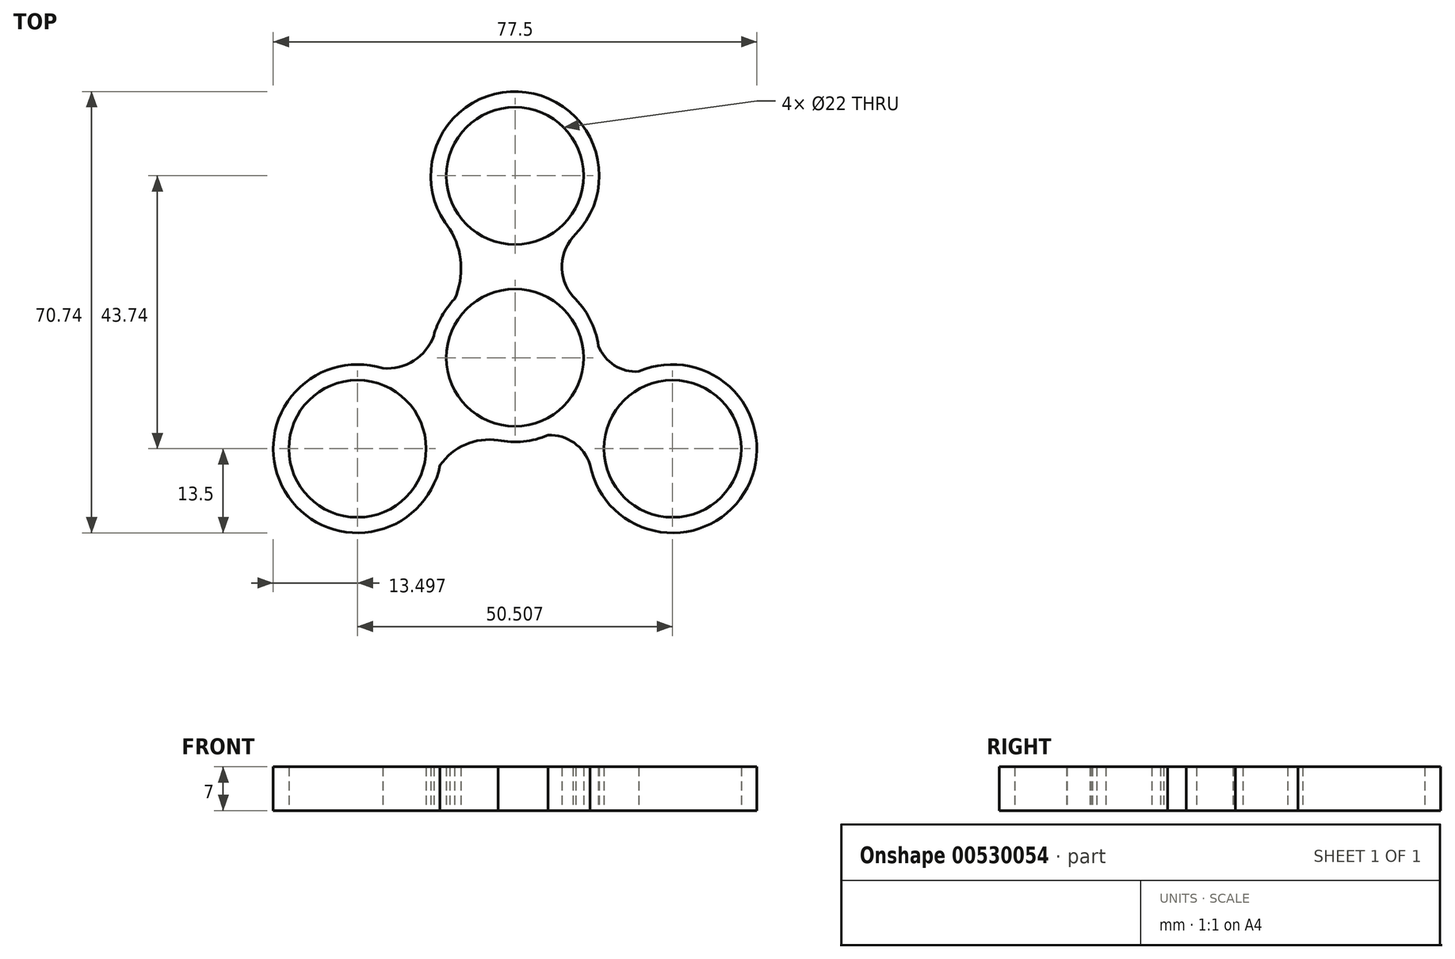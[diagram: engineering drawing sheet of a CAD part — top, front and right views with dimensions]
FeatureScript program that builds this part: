
annotation { "Feature Type Name" : "Feature", "Feature Type Description" : "" }
export const myFeature = defineFeature(function(context is Context, id is Id, definition is map)
    precondition{}
    {
        {
            var Q0;
            Q0=qCreatedBy(makeId("Top.planeOp"),FACE);
            var sketch = newSketch(context, id + "F0", { "sketchPlane" : qUnion([Q0])});
            skCircle(sketch, "E0", {"center": v(0, 0) * mm, "radius": 11 * mm});
            skCircle(sketch, "E1", {"center": v(0, 0) * mm, "radius": 13.5 * mm});
            skCircle(sketch, "E2", {"center": v(0, 29.16) * mm, "radius": 11 * mm});
            skCircle(sketch, "E3", {"center": v(0, 29.16) * mm, "radius": 13.5 * mm});
            skCircle(sketch, "E4.1.0", {"center": v(-25.25, -14.58) * mm, "radius": 11 * mm});
            skCircle(sketch, "E4.2.0", {"center": v(25.25, -14.58) * mm, "radius": 11 * mm});
            skCircle(sketch, "E5.1.0", {"center": v(-25.25, -14.58) * mm, "radius": 13.5 * mm});
            skCircle(sketch, "E5.2.0", {"center": v(25.25, -14.58) * mm, "radius": 13.5 * mm});
            skArc(sketch, "E6", {"start": v(-9.69, 9.4) * mm, "mid": v(-8.68, 15.1) * mm, "end": v(-10.44, 20.6) * mm});
            skArc(sketch, "E7", {"start": v(9.76, 19.84) * mm, "mid": v(7.53, 14.92) * mm, "end": v(9.27, 9.81) * mm});
            skArc(sketch, "E8", {"start": v(-21.2, -1.7) * mm, "mid": v(-16.22, -0.47) * mm, "end": v(-13.03, 3.55) * mm});
            skArc(sketch, "E9", {"start": v(-2.71, -13.22) * mm, "mid": v(-7.94, -13.91) * mm, "end": v(-12.02, -17.25) * mm});
            skArc(sketch, "E10", {"start": v(12, -17.17) * mm, "mid": v(9.46, -13.64) * mm, "end": v(5.28, -12.43) * mm});
            skArc(sketch, "E11", {"start": v(13.36, 1.91) * mm, "mid": v(15.92, -1.22) * mm, "end": v(19.84, -2.21) * mm});
            skSolve(sketch);
        }
        {
            var Q0;
            Q0=makeQuery(id+"F0.imprint","IMPRINT",FACE,{"disambiguationData":[TD([[makeQuery(id+"F0.imprint","IMPRINT",EDGE,{"derivedFrom":sQuery(id+"F0.wireOp",EDGE,"E2")}),-1.0]])]});
            var Q1;
            Q1=makeQuery(id+"F0.imprint","IMPRINT",FACE,{"disambiguationData":[TD([[makeQuery(id+"F0.imprint","IMPRINT",EDGE,{"derivedFrom":sQuery(id+"F0.wireOp",EDGE,"E0")}),-1.0]])]});
            var Q2;
            Q2=makeQuery(id+"F0.imprint","IMPRINT",FACE,{"disambiguationData":[TD([[makeQuery(id+"F0.imprint","IMPRINT",EDGE,{"derivedFrom":sQuery(id+"F0.wireOp",EDGE,"E4.1.0")}),-1.0]])]});
            var Q3;
            Q3=makeQuery(id+"F0.imprint","IMPRINT",FACE,{"disambiguationData":[TD([[makeQuery(id+"F0.imprint","IMPRINT",EDGE,{"derivedFrom":sQuery(id+"F0.wireOp",EDGE,"E4.2.0")}),-1.0]])]});
            var Q4;
            {var subQ0=sQuery(id+"F0.wireOp",EDGE,"E10");Q4=makeQuery(id+"F0.imprint","IMPRINT",FACE,{"disambiguationData":[TD([[makeQuery(id+"F0.imprint","IMPRINT",EDGE,{"derivedFrom":subQ0}),-1.0]])]});}
            var Q5;
            {var subQ0=sQuery(id+"F0.wireOp",EDGE,"E8");Q5=makeQuery(id+"F0.imprint","IMPRINT",FACE,{"disambiguationData":[TD([[makeQuery(id+"F0.imprint","IMPRINT",EDGE,{"derivedFrom":subQ0}),-1.0]])]});}
            var Q6;
            {var subQ0=sQuery(id+"F0.wireOp",EDGE,"E6");Q6=makeQuery(id+"F0.imprint","IMPRINT",FACE,{"disambiguationData":[TD([[makeQuery(id+"F0.imprint","IMPRINT",EDGE,{"derivedFrom":subQ0}),-1.0]])]});}
            extrude(context, id + "F1", {"entities" : qUnion([Q0, Q1, Q2, Q3, Q4, Q5, Q6]), "depth" : 7 * mm});
        }
    });
